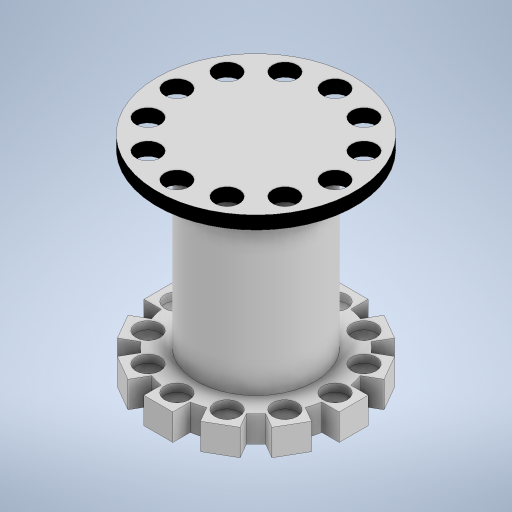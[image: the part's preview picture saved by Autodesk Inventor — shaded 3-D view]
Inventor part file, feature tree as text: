
AUTODESK INVENTOR PART (.ipt)
format: ipt  version: 2023 (Build 270158000, 158)  size: 470,016 bytes
history: native  units: mm
features: sketch x5, extrude x4, fillet x1
ambient origin geometry x8: Origin, YZ Plane, XZ Plane, XY Plane, X Axis, Y Axis, Z Axis, Center Point
bodies: Solid1 (feature_tree)
feature tree (10):
  extrude  "Extrusion1"  Depth=150.0mm
  extrude  "Extrusion2"  Depth=120.0mm TaperAngle=360.0deg
  extrude  "Extrusion9"  Depth=10.0mm
  extrude  "Extrusion10"  Depth=20.0mm TaperAngle=360.0deg
  fillet  "Fillet1"  Radius=20.0mm
  sketch  "Sketch8"  dims[d71=120.0mm d72=18.5mm d73=120.0mm d75=360.0deg d77=10.0mm d78=0.0mm d91=4.0mm d92=124.403mm d93=23.006mm d94=14.13mm d95=0.5mm d97=14.13mm d98=0.5mm d99=120.0mm d101=360.0deg]
  sketch  "Sketch1"  dims[d0=150.0mm d1=120.0mm]
  sketch  "Sketch2"  dims[d2=18.5mm d3=120.0mm d5=360.0deg]
  sketch  "Sketch3"  dims[d7=10.0mm d8=0.0mm d9=90.0mm]
  sketch  "Sketch7"  dims[d10=130.0mm d11=0.0mm d67=120.0mm d68=360.0deg d69=20.0mm d70=0.0mm]
